# Revit family: 0043514
name_source: partatom
category: Lighting Fixtures
revit_build: Autodesk Revit 2017 (Build: 20190507_1515(x64)
units: mm (PartAtom-declared; Revit-internal decimal feet)

## family parameters
Cut with Voids When Loaded = No
Host = Face
Light Source = Yes
OmniClass Number = 23.80.70.00
OmniClass Title = Lighting
Part Type = Normal
Room Calculation Point = No
Round Connector Dimension = Use Diameter
Shared = No

## types (2) — shared parameters
00_220_SYL = No
00_280_SYL = Yes
00_330_SYL = No
00_400_SYL = No
Apparent Load = 18 VA
Assembly Code = D5020200
AssetType = Fixed
ClassificationName = Uniclass2015
ClassificationValue = EF_70_80
Color Filter = 16777215
Default Elevation = 1219 mm
Description = Ceiling / wall round luminaire with integrated LED. Perfect solution for corridors, circulation areas or bathrooms. Even and uniform light in a slim but robust design. Power W, lumen output  lumens, lumen efficacy  lm/W, dual color temperature (3000K/4000K). Supplied with phase dimming driver (leading edge/trailing edge). Mains Voltage . Body Size: mm diameter x mm height. ,  Protection rating.   diffuser.Low maintenance with  hours LED life expectancy. Warranty: 3 years.
Dimming Lamp Color Temperature Shift = <None>
DocumentationLiterature = http://www.sylvania-lighting.com
ElectricShockClassification = Class II
Emit Shape Visible in Rendering = No
Emit from Circle Diameter = 610 mm
IfcExportAs = IfcLightFixtureType
IfcExportType = IfcLightFixtureType
ImpactProtectionIndex = IK07
IngressProtection = IP54
Keynote = 16500
LUM_H2_SYL = 32 mm
LUM_H_SYL = 53 mm  [stored 0.173885 ft]
LUM_R2_SYL = 123 mm  [stored 0.403543 ft]
LUM_R_SYL = 140 mm  [stored 0.459318 ft]
Lamp = LED
LampColourRenderingIndex = 80
LampMacAdamStep = 3
LampNominalLuminous = 1900 lm
LampsType = LED
LuminousEfficacy = 95 lm/W
Manufacturer = Feilo Sylvania
ManufacturerName = Feilo Sylvania
Material = pc polycarbonate housing, pc polycarbonate diffuser
Material_1_SYL = <By Category>
Material_2_SYL = <By Category>
Material_3_SYL = <By Category>
Material_4_SYL = <By Category>
Model = START SURFACE SLIM IP54 ROUND 1900LM 2CCT D MW WH
ModelNumber = 0043514
ModelReference = START SURFACE SLIM IP54 ROUND 1900LM 2CCT D MW WH
Name = START SURFACE SLIM IP54 ROUND 1900LM 2CCT D MW WH
NominalDepth = 280 mm
NominalHeight = 53 mm  [stored 0.173885 ft]
NominalLength = 280 mm
PowerConsumption = 18 W
PowerFactor = 0.9
Tilt Angle = -90.00°
Type Image = <None>
TypeName = START SURFACE SLIM IP54 ROUND 1900LM 2CCT D MW WH
URL = http://www.sylvania-lighting.com
Voltage = 0 V
zero-valued in all types: Cost

## per-type parameters (varying)
| type | LampColourTemperature | Photometric Web File |
| 0043514_3000K START SURF SLIM IP54 R 1900 2CCT D MW WH | 3000 K | 0043514_3000K.IES |
| 0043514_4000K START SURF SLIM IP54 R 1900 2CCT D MW WH | 4000 K | 0043514_4000K.ies |

note: [stored X ft] marks values corroborated as IEEE doubles in the binary element streams (Revit-internal decimal feet)

## geometry (parser evidence)
native form markers: Sweep x2
no freeform markers — native parametric forms only
